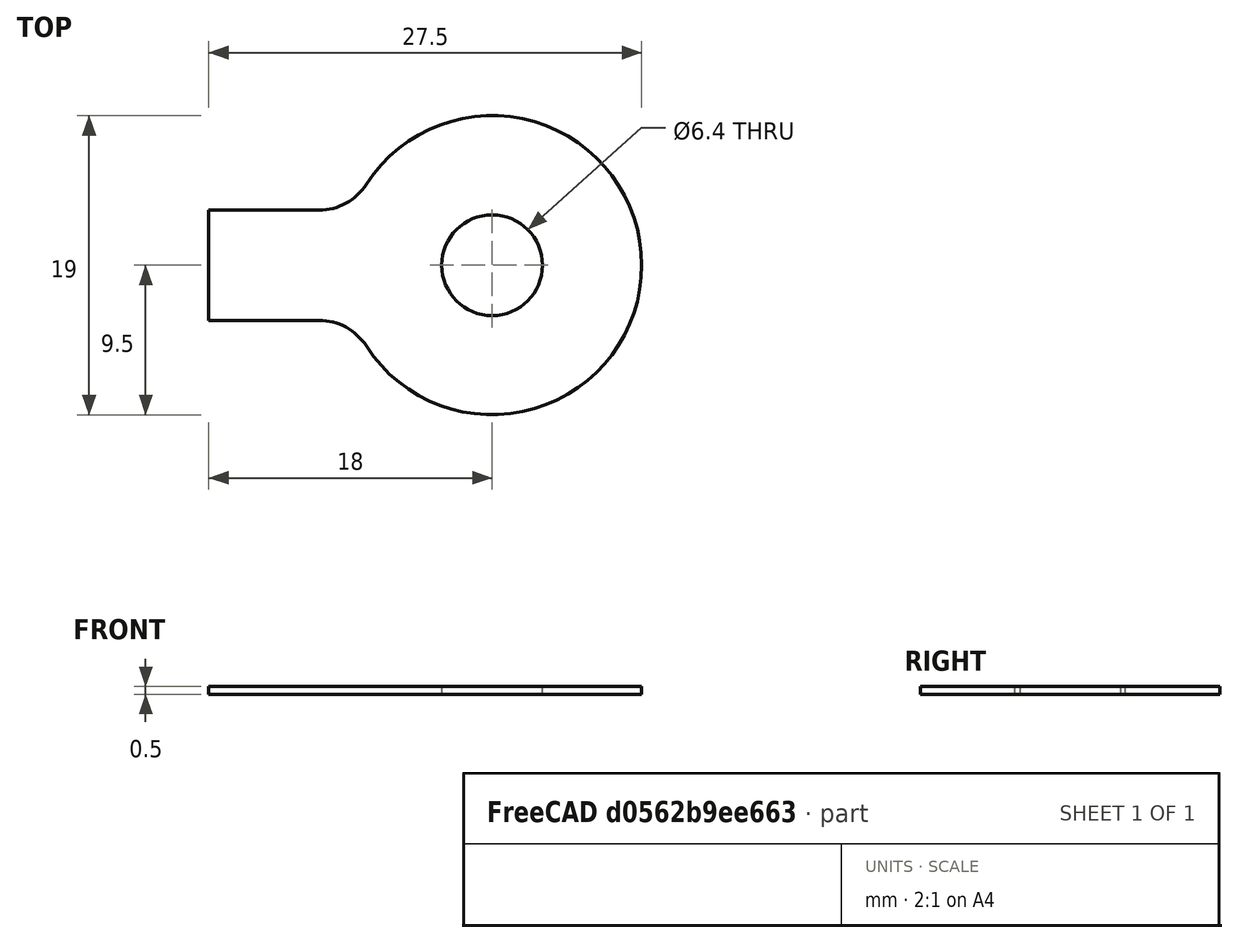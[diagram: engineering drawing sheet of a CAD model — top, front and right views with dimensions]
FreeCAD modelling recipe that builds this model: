
FCSTD DOCUMENT  (FreeCAD 0.15R4671 (Git))
Label: DIN93_M6TabWasher
License: CreativeCommons Attribution-ShareAlike
LicenseURL: http://creativecommons.org/licenses/by-sa/4.0/
objects: Sketcher::SketchObject×1, PartDesign::Pad×1
note: 3 computed .brp shape members not serialized (recipe doc carries the construction recipe); baked Part::Feature solids carry a one-line shape summary decoded from their .brp

FEATURE [Sketcher::SketchObject] Sketch
  sketch-geometry (7):
    g0: Circle CenterX=0 CenterY=0 CenterZ=0 NormalX=0 NormalY=0 NormalZ=1 Radius=3.2
    g1: LineSegment StartX=-18 StartY=3.5 StartZ=0 EndX=-11 EndY=3.5 EndZ=0
    g2: LineSegment StartX=-11 StartY=-3.5 StartZ=0 EndX=-18 EndY=-3.5 EndZ=0
    g3: LineSegment StartX=-18 StartY=-3.5 StartZ=0 EndX=-18 EndY=3.5 EndZ=0
    g4: ArcOfCircle CenterX=0 CenterY=0 CenterZ=0 NormalX=0 NormalY=0 NormalZ=1 Radius=9.5 StartAngle=3.7137 EndAngle=8.85267
    g5: ArcOfCircle CenterX=-11 CenterY=7.08334 CenterZ=0 NormalX=0 NormalY=0 NormalZ=1 Radius=3.58334 StartAngle=4.71239 EndAngle=5.71109
    g6: ArcOfCircle CenterX=-11 CenterY=-7.08334 CenterZ=0 NormalX=0 NormalY=0 NormalZ=1 Radius=3.58334 StartAngle=0.5721 EndAngle=1.5708
  constraints (22):
    c: Coincident(g0,g-1)
    c: Radius(g0) = 3.2
    c: Coincident(g2,g3)
    c: Coincident(g3,g1)
    c: Horizontal(g1)
    c: Horizontal(g2)
    c: Vertical(g3)
    c: Symmetric(g1,g2,g-1)
    c: Equal(g1,g3)
    c: Equal(g3,g2)
    c: DistanceY(g3) = 7
    c: DistanceX(g-1,g2) = -18
    c: Coincident(g4,g-1)
    c: Radius(g4) = 9.5
    c: Coincident(g5,g4)
    c: Coincident(g5,g1)
    c: Tangent(g5,g4)
    c: Coincident(g6,g2)
    c: Coincident(g6,g4)
    c: Tangent(g4,g6)
    c: Tangent(g6,g2)
    c: Tangent(g1,g5)
FEATURE [PartDesign::Pad] Pad
  Length = 0.5
  Length2 = 100
  Sketch = -> Sketch
  Type = 0
